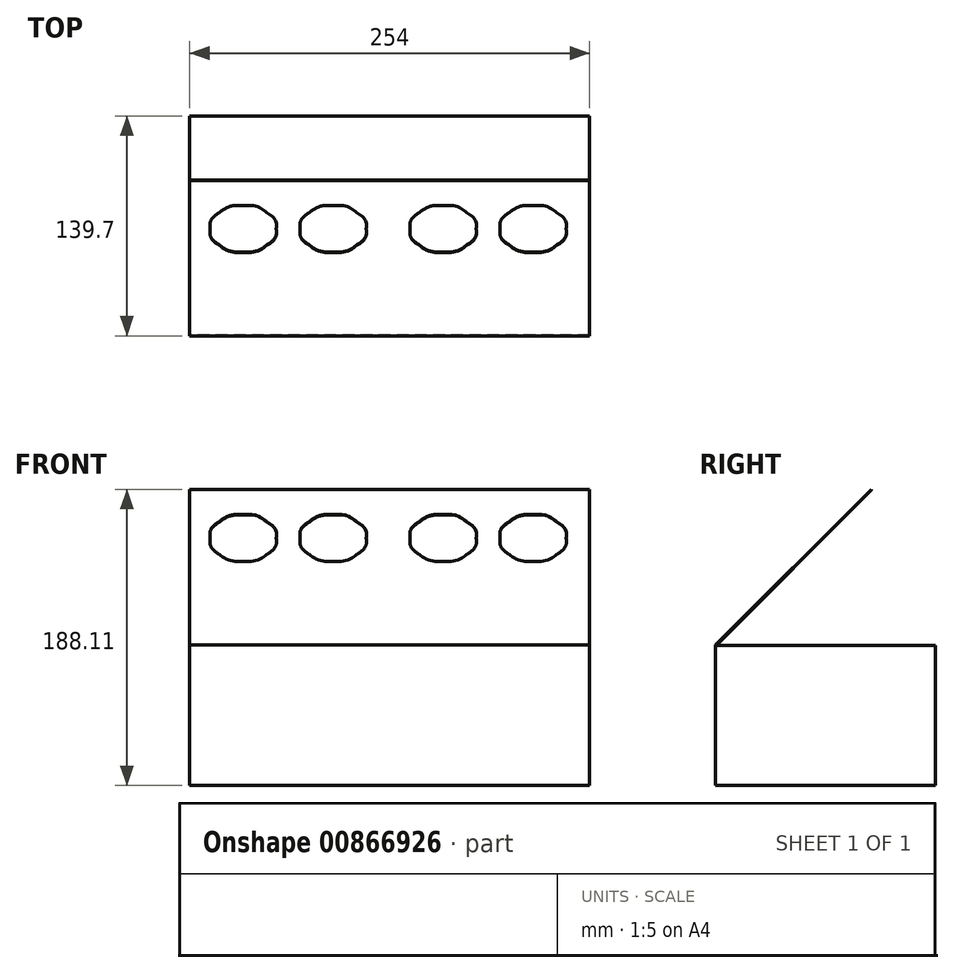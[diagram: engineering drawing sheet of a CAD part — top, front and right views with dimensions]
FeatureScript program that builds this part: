
annotation { "Feature Type Name" : "Feature", "Feature Type Description" : "" }
export const myFeature = defineFeature(function(context is Context, id is Id, definition is map)
    precondition{}
    {
        {
            var Q0;
            Q0=qCreatedBy(makeId("Right.planeOp"),FACE);
            var sketch = newSketch(context, id + "F0", { "sketchPlane" : qUnion([Q0])});
            skLineSegment(sketch, "E0.bottom", {"start": v(0, 0) * mm, "end": v(-139.7, 0) * mm});
            skLineSegment(sketch, "E0.top", {"start": v(0, 88.9) * mm, "end": v(-139.3, 88.9) * mm});
            skLineSegment(sketch, "E0.left", {"start": v(0, 0) * mm, "end": v(0, 88.9) * mm});
            skLineSegment(sketch, "E0.right", {"start": v(-139.7, 0) * mm, "end": v(-139.7, 89.32) * mm});
            skLineSegment(sketch, "E1", {"start": v(-139.7, 89.32) * mm, "end": v(-40.92, 188.1) * mm});
            skLineSegment(sketch, "E2", {"start": v(-40.92, 188.1) * mm, "end": v(-40.63, 187.82) * mm});
            skLineSegment(sketch, "E3", {"start": v(-40.63, 187.82) * mm, "end": v(-139.3, 89.15) * mm});
            skLineSegment(sketch, "E4", {"start": v(-139.3, 88.9) * mm, "end": v(-139.3, 89.15) * mm});
            skLineSegment(sketch, "E5", {"start": v(-139.3, 88.9) * mm, "end": v(-139.7, 88.9) * mm, "construction": true});
            skSolve(sketch);
        }
        {
            var Q0;
            Q0=qSketchRegion(id+"F0",true);
            extrude(context, id + "F1", {"entities" : qUnion([Q0]), "endBound" : BoundingType.SYMMETRIC, "depth" : 254 * mm, "offsetDistance" : 25.4 * mm});
        }
        {
            var Q0;
            Q0=makeQuery(id+"F1.opExtrude","SWEPT_FACE",FACE,{"disambiguationData":[OSD([sQuery(id+"F0.wireOp",EDGE,"E1")])]});
            var sketch = newSketch(context, id + "F2", { "sketchPlane" : qUnion([Q0])});
            skLineSegment(sketch, "E6", {"start": v(126, -34.03) * mm, "end": v(126, 104.88) * mm, "construction": true});
            skLineSegment(sketch, "E7", {"start": v(-128, 104.88) * mm, "end": v(126, 104.88) * mm, "construction": true});
            skLineSegment(sketch, "E8", {"start": v(-128, -34.03) * mm, "end": v(-128, 104.88) * mm, "construction": true});
            skLineSegment(sketch, "E9", {"start": v(126, -34.03) * mm, "end": v(-128, -34.03) * mm, "construction": true});
            skFitSpline(sketch, "E10", {"points": [v(-35.96, 81.48) * mm, v(-41.47, 81.48) * mm, v(-46.94, 79.22) * mm, v(-50.84, 75.32) * mm]});
            skFitSpline(sketch, "E11", {"points": [v(-50.84, 75.32) * mm, v(-54.73, 71.43) * mm, v(-57, 65.96) * mm, v(-57, 60.45) * mm, v(-57, 54.94) * mm, v(-54.73, 49.47) * mm, v(-50.84, 45.58) * mm]});
            skFitSpline(sketch, "E12", {"points": [v(-50.84, 45.58) * mm, v(-46.94, 41.68) * mm, v(-41.47, 39.42) * mm, v(-35.96, 39.42) * mm, v(-30.46, 39.42) * mm, v(-24.98, 41.68) * mm, v(-21.09, 45.58) * mm]});
            skFitSpline(sketch, "E13", {"points": [v(-21.09, 45.58) * mm, v(-17.2, 49.47) * mm, v(-14.93, 54.94) * mm, v(-14.93, 60.45) * mm, v(-14.93, 65.96) * mm, v(-17.2, 71.43) * mm, v(-21.09, 75.32) * mm, v(-24.98, 79.22) * mm, v(-30.46, 81.48) * mm, v(-35.96, 81.48) * mm]});
            skFitSpline(sketch, "E14", {"points": [v(33.89, 81.48) * mm, v(28.38, 81.48) * mm, v(22.9, 79.22) * mm, v(19.01, 75.32) * mm]});
            skFitSpline(sketch, "E15", {"points": [v(19.01, 75.32) * mm, v(15.12, 71.43) * mm, v(12.85, 65.96) * mm, v(12.85, 60.45) * mm, v(12.85, 54.94) * mm, v(15.12, 49.47) * mm, v(19.01, 45.58) * mm]});
            skFitSpline(sketch, "E16", {"points": [v(19.01, 45.58) * mm, v(22.9, 41.68) * mm, v(28.38, 39.42) * mm, v(33.89, 39.42) * mm, v(39.4, 39.42) * mm, v(44.87, 41.68) * mm, v(48.76, 45.58) * mm]});
            skFitSpline(sketch, "E17", {"points": [v(48.76, 45.58) * mm, v(52.66, 49.47) * mm, v(54.92, 54.94) * mm, v(54.92, 60.45) * mm, v(54.92, 65.96) * mm, v(52.66, 71.43) * mm, v(48.76, 75.32) * mm, v(44.87, 79.22) * mm, v(39.4, 81.48) * mm, v(33.89, 81.48) * mm]});
            skFitSpline(sketch, "E18", {"points": [v(91.04, 81.48) * mm, v(85.53, 81.48) * mm, v(80.06, 79.22) * mm, v(76.16, 75.32) * mm]});
            skFitSpline(sketch, "E19", {"points": [v(76.16, 75.32) * mm, v(72.27, 71.43) * mm, v(70, 65.96) * mm, v(70, 60.45) * mm, v(70, 54.94) * mm, v(72.27, 49.47) * mm, v(76.16, 45.58) * mm]});
            skFitSpline(sketch, "E20", {"points": [v(76.16, 45.58) * mm, v(80.06, 41.68) * mm, v(85.53, 39.42) * mm, v(91.04, 39.42) * mm, v(96.54, 39.42) * mm, v(102.02, 41.68) * mm, v(105.91, 45.58) * mm]});
            skFitSpline(sketch, "E21", {"points": [v(105.91, 45.58) * mm, v(109.8, 49.47) * mm, v(112.07, 54.94) * mm, v(112.07, 60.45) * mm, v(112.07, 65.96) * mm, v(109.8, 71.43) * mm, v(105.91, 75.32) * mm, v(102.02, 79.22) * mm, v(96.54, 81.48) * mm, v(91.04, 81.48) * mm]});
            skFitSpline(sketch, "E22", {"points": [v(-93.11, 81.48) * mm, v(-98.62, 81.48) * mm, v(-104.1, 79.22) * mm, v(-107.99, 75.32) * mm]});
            skFitSpline(sketch, "E23", {"points": [v(-107.99, 75.32) * mm, v(-111.88, 71.43) * mm, v(-114.15, 65.96) * mm, v(-114.15, 60.45) * mm, v(-114.15, 54.94) * mm, v(-111.88, 49.47) * mm, v(-107.99, 45.58) * mm]});
            skFitSpline(sketch, "E24", {"points": [v(-107.99, 45.58) * mm, v(-104.1, 41.68) * mm, v(-98.62, 39.42) * mm, v(-93.11, 39.42) * mm, v(-87.6, 39.42) * mm, v(-82.13, 41.68) * mm, v(-78.24, 45.58) * mm]});
            skFitSpline(sketch, "E25", {"points": [v(-78.24, 45.58) * mm, v(-74.34, 49.47) * mm, v(-72.08, 54.94) * mm, v(-72.08, 60.45) * mm, v(-72.08, 65.96) * mm, v(-74.34, 71.43) * mm, v(-78.24, 75.32) * mm, v(-82.13, 79.22) * mm, v(-87.6, 81.48) * mm, v(-93.11, 81.48) * mm]});
            skSolve(sketch);
        }
        {
            var Q0;
            Q0=qSketchRegion(id+"F2",true);
            var Q1;
            Q1=makeQuery(id+"F1.opExtrude","SWEPT_FACE",FACE,{"disambiguationData":[OSD([sQuery(id+"F0.wireOp",EDGE,"E3")])]});
            extrude(context, id + "F3", {"entities" : qUnion([Q0]), "operationType" : NewBodyOperationType.REMOVE, "endBound" : BoundingType.UP_TO_SURFACE, "oppositeDirection" : true, "depth" : 25.4 * mm, "endBoundEntityFace" : qUnion([Q1]), "offsetDistance" : 25.4 * mm});
        }
    });
